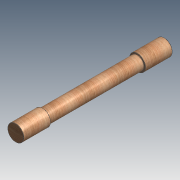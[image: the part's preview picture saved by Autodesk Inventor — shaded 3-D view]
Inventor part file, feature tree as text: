
AUTODESK INVENTOR PART (.ipt)
format: ipt  version: 2015 (Build 190159000, 159)  size: 125,952 bytes
history: native  units: mm
features: fillet x5, extrude x3, sketch x3
ambient origin geometry x8: Origin, YZ Plane, XZ Plane, XY Plane, X Axis, Y Axis, Z Axis, Center Point
bodies: Solid1 (feature_tree)
feature tree (11):
  extrude  "Extrusion1"  Depth=200.0mm TaperAngle=0.0deg
  extrude  "Extrusion2"  Depth=700.0mm TaperAngle=0.0deg
  extrude  "Extrusion3"  Depth=200.0mm TaperAngle=0.0deg
  fillet  "Fillet1"  Radius=2.0mm
  fillet  "Fillet2"  Radius=2.0mm
  fillet  "Fillet3"  Radius=2.0mm
  fillet  "Fillet4"  Radius=2.0mm
  fillet  "Fillet5"  Radius=2.0mm
  sketch  "Sketch1"  dims[d0=120.0mm d1=200.0mm d2=0.0mm]
  sketch  "Sketch2"  dims[d3=100.0mm d4=700.0mm d5=0.0mm]
  sketch  "Sketch3"  dims[d6=120.0mm d7=200.0mm d8=0.0mm d9=2.0mm d10=2.0mm d11=2.0mm d12=2.0mm d13=2.0mm]
